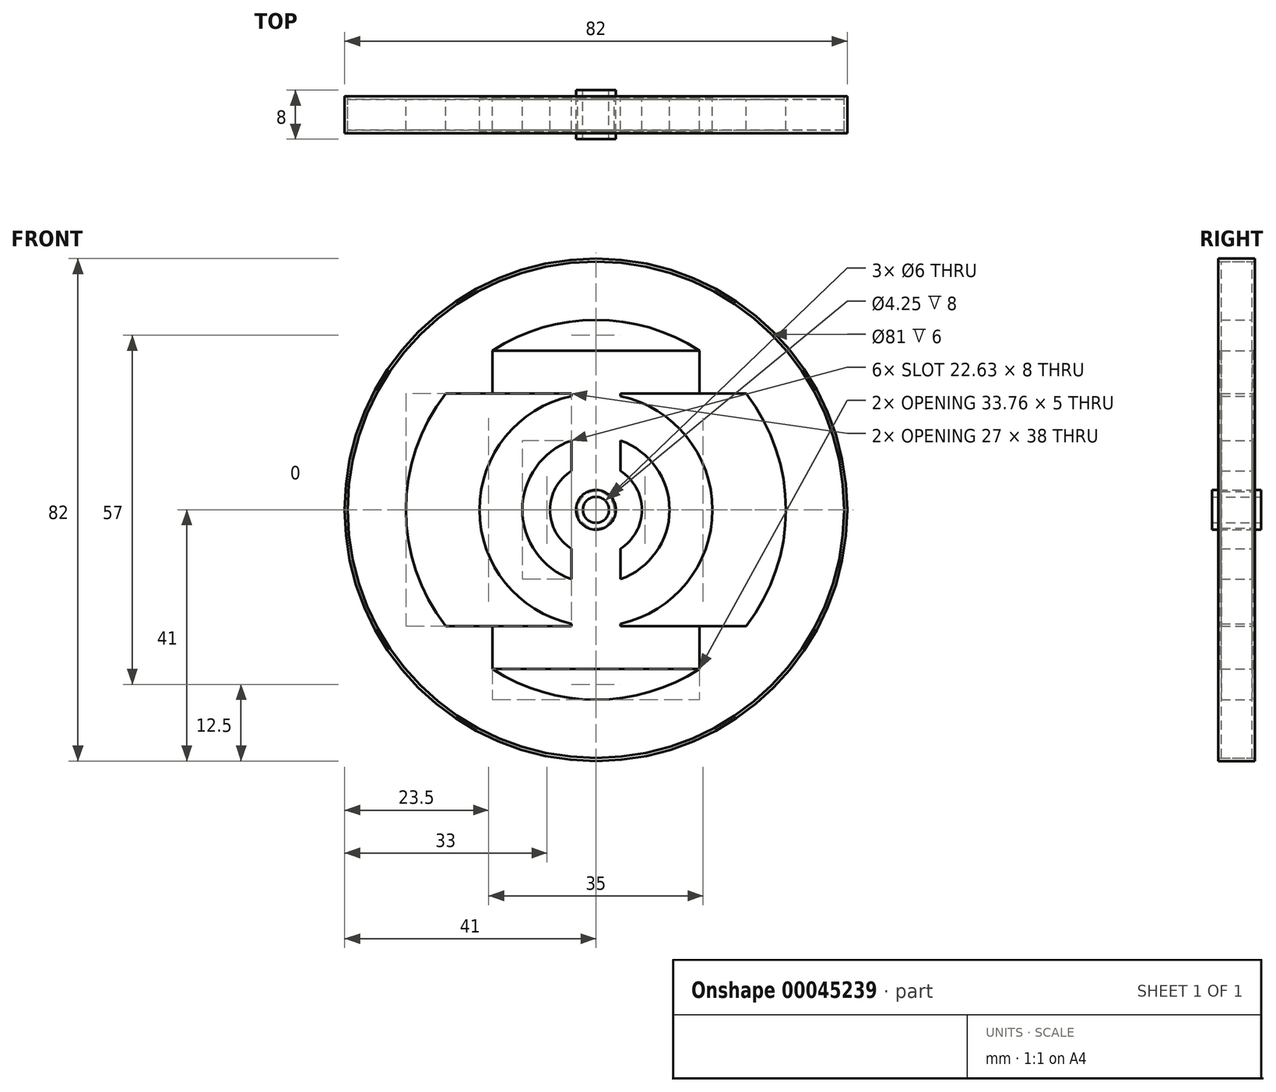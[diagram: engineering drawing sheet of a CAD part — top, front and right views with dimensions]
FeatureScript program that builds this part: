
annotation { "Feature Type Name" : "Feature", "Feature Type Description" : "" }
export const myFeature = defineFeature(function(context is Context, id is Id, definition is map)
    precondition{}
    {
        {
            var Q0;
            Q0=qCreatedBy(makeId("Front.planeOp"),FACE);
            var sketch = newSketch(context, id + "F0", { "sketchPlane" : qUnion([Q0])});
            skCircle(sketch, "E0", {"center": v(0, 0) * mm, "radius": 40.5 * mm});
            skArc(sketch, "E1", {"start": v(16.88, 26) * mm, "mid": v(0, 31) * mm, "end": v(-16.88, 26) * mm});
            skLineSegment(sketch, "E2", {"start": v(0, 40.5) * mm, "end": v(0, -40.5) * mm, "construction": true});
            skArc(sketch, "E3", {"start": v(-4, 11.31) * mm, "mid": v(-12, 0) * mm, "end": v(-4, -11.31) * mm});
            skArc(sketch, "E4", {"start": v(-4, 6.34) * mm, "mid": v(-7.5, 0) * mm, "end": v(-4, -6.34) * mm});
            skCircle(sketch, "E5", {"center": v(0, 0) * mm, "radius": 3 * mm});
            skArc(sketch, "E6", {"start": v(-4, 18.57) * mm, "mid": v(-19, 0) * mm, "end": v(-4, -18.57) * mm});
            skArc(sketch, "E7.trimOffspring", {"start": v(24.5, -19) * mm, "mid": v(31, 0) * mm, "end": v(24.5, 19) * mm});
            skArc(sketch, "E8.trimOffspring", {"start": v(4, -6.34) * mm, "mid": v(7.5, 0) * mm, "end": v(4, 6.34) * mm});
            skArc(sketch, "E9.trimOffspring", {"start": v(4, -11.31) * mm, "mid": v(12, 0) * mm, "end": v(4, 11.31) * mm});
            skLineSegment(sketch, "E10.trimOffspring", {"start": v(-4, -6.34) * mm, "end": v(-4, -11.31) * mm});
            skLineSegment(sketch, "E11.trimOffspring", {"start": v(4, -6.34) * mm, "end": v(4, -11.31) * mm});
            skLineSegment(sketch, "E12.trimOffspring", {"start": v(4, 11.31) * mm, "end": v(4, 6.34) * mm});
            skLineSegment(sketch, "E13.trimOffspring", {"start": v(-4, 11.31) * mm, "end": v(-4, 6.34) * mm});
            skLineSegment(sketch, "E14.trimOffspring", {"start": v(-4, -18.57) * mm, "end": v(-4, -19) * mm});
            skLineSegment(sketch, "E15.trimOffspring", {"start": v(4, -18.57) * mm, "end": v(4, -19) * mm});
            skLineSegment(sketch, "E16.bottom", {"start": v(-24.5, 19) * mm, "end": v(-4, 19) * mm});
            skLineSegment(sketch, "E16.top", {"start": v(-16.88, 26) * mm, "end": v(16.88, 26) * mm});
            skArc(sketch, "E17.trimOffspring", {"start": v(-24.5, 19) * mm, "mid": v(-31, 0) * mm, "end": v(-24.5, -19) * mm});
            skLineSegment(sketch, "E18.trimOffspring", {"start": v(-4, 19) * mm, "end": v(-4, 18.57) * mm});
            skLineSegment(sketch, "E19.trimOffspring", {"start": v(4, 19) * mm, "end": v(4, 18.57) * mm});
            skLineSegment(sketch, "E20.trimOffspring", {"start": v(4, 19) * mm, "end": v(24.5, 19) * mm});
            skLineSegment(sketch, "E21", {"start": v(-40.5, 0) * mm, "end": v(40.5, 0) * mm, "construction": true});
            skLineSegment(sketch, "E22.MirrorCS", {"start": v(-24.5, -19) * mm, "end": v(-4, -19) * mm});
            skLineSegment(sketch, "E23.MirrorCS", {"start": v(-16.88, -26) * mm, "end": v(16.88, -26) * mm});
            skArc(sketch, "E24.MirrorCS", {"start": v(16.88, -26) * mm, "mid": v(0, -31) * mm, "end": v(-16.88, -26) * mm});
            skLineSegment(sketch, "E25.MirrorCS", {"start": v(4, -19) * mm, "end": v(24.5, -19) * mm});
            skArc(sketch, "E26.trimOffspring", {"start": v(4, -18.57) * mm, "mid": v(19, 0) * mm, "end": v(4, 18.57) * mm});
            skPoint(sketch, "E27.trimOffspring.end.orphan", {"position": v(-16.88, -26) * mm});
            skSolve(sketch);
        }
        {
            var Q0;
            Q0=makeQuery(id+"F0.imprint","IMPRINT",FACE,{"disambiguationData":[TD([[makeQuery(id+"F0.imprint","IMPRINT",EDGE,{"derivedFrom":sQuery(id+"F0.wireOp",EDGE,"E0")}),1.0]])]});
            extrude(context, id + "F1", {"entities" : qUnion([Q0]), "endBound" : BoundingType.SYMMETRIC, "depth" : 5 * mm});
        }
        {
            var Q0;
            Q0=qCreatedBy(makeId("Front.planeOp"),FACE);
            var sketch = newSketch(context, id + "F2", { "sketchPlane" : qUnion([Q0])});
            skCircle(sketch, "E28.0", {"center": v(0, 0) * mm, "radius": 41 * mm});
            skCircle(sketch, "E29.0", {"center": v(0, 0) * mm, "radius": 40.5 * mm});
            skSolve(sketch);
        }
        {
            var Q0;
            Q0 = qSketchRegion(id + "F2", true);
            extrude(context, id + "F3", {"entities" : qUnion([Q0]), "endBound" : BoundingType.SYMMETRIC, "depth" : 6 * mm});
        }
        {
            var Q0;
            Q0=qCreatedBy(makeId("Front.planeOp"),FACE);
            var sketch = newSketch(context, id + "F4", { "sketchPlane" : qUnion([Q0])});
            skCircle(sketch, "E30", {"center": v(0, 0) * mm, "radius": 3.25 * mm});
            skCircle(sketch, "E31", {"center": v(0, 0) * mm, "radius": 2.12 * mm});
            skSolve(sketch);
        }
        {
            var Q0;
            Q0 = qSketchRegion(id + "F4", true);
            extrude(context, id + "F5", {"entities" : qUnion([Q0]), "endBound" : BoundingType.SYMMETRIC, "depth" : 8 * mm});
        }
        {
            var Q0;
            Q0=makeQuery(id+"F1.opExtrude","CAP_FACE",FACE,{"disambiguationData":[OSD([sQuery(id+"F0.wireOp",EDGE,"E0"),sQuery(id+"F0.wireOp",EDGE,"E1"),sQuery(id+"F0.wireOp",EDGE,"E3"),sQuery(id+"F0.wireOp",EDGE,"E4"),sQuery(id+"F0.wireOp",EDGE,"E5"),sQuery(id+"F0.wireOp",EDGE,"E6"),sQuery(id+"F0.wireOp",EDGE,"E7.trimOffspring"),sQuery(id+"F0.wireOp",EDGE,"E8.trimOffspring"),sQuery(id+"F0.wireOp",EDGE,"E9.trimOffspring"),sQuery(id+"F0.wireOp",EDGE,"E10.trimOffspring"),sQuery(id+"F0.wireOp",EDGE,"E11.trimOffspring"),sQuery(id+"F0.wireOp",EDGE,"E12.trimOffspring"),sQuery(id+"F0.wireOp",EDGE,"E13.trimOffspring"),sQuery(id+"F0.wireOp",EDGE,"E14.trimOffspring"),sQuery(id+"F0.wireOp",EDGE,"E15.trimOffspring"),sQuery(id+"F0.wireOp",EDGE,"E16.bottom"),sQuery(id+"F0.wireOp",EDGE,"E16.top"),sQuery(id+"F0.wireOp",EDGE,"E17.trimOffspring"),sQuery(id+"F0.wireOp",EDGE,"E18.trimOffspring"),sQuery(id+"F0.wireOp",EDGE,"E19.trimOffspring"),sQuery(id+"F0.wireOp",EDGE,"E20.trimOffspring"),sQuery(id+"F0.wireOp",EDGE,"E22.MirrorCS"),sQuery(id+"F0.wireOp",EDGE,"E23.MirrorCS"),sQuery(id+"F0.wireOp",EDGE,"E24.MirrorCS"),sQuery(id+"F0.wireOp",EDGE,"E25.MirrorCS"),sQuery(id+"F0.wireOp",EDGE,"E26.trimOffspring")])],"isStart":false});
            var sketch = newSketch(context, id + "F6", { "sketchPlane" : qUnion([Q0])});
            skLineSegment(sketch, "E32.0", {"start": v(-16.88, 26) * mm, "end": v(16.88, 26) * mm});
            skLineSegment(sketch, "E32.1", {"start": v(4, 19) * mm, "end": v(16.88, 19) * mm});
            skLineSegment(sketch, "E32.2", {"start": v(-16.88, 19) * mm, "end": v(-4, 19) * mm});
            skLineSegment(sketch, "E32.3", {"start": v(4, 19) * mm, "end": v(4, 18.57) * mm});
            skLineSegment(sketch, "E32.4", {"start": v(-4, 19) * mm, "end": v(-4, 18.57) * mm});
            skArc(sketch, "E32.5", {"start": v(-4, 18.57) * mm, "mid": v(-19, 0) * mm, "end": v(-4, -18.57) * mm});
            skArc(sketch, "E32.6", {"start": v(4, -18.57) * mm, "mid": v(19, 0) * mm, "end": v(4, 18.57) * mm});
            skArc(sketch, "E32.7", {"start": v(4, -11.31) * mm, "mid": v(12, 0) * mm, "end": v(4, 11.31) * mm});
            skLineSegment(sketch, "E32.8", {"start": v(4, 11.31) * mm, "end": v(4, 6.34) * mm});
            skLineSegment(sketch, "E32.9", {"start": v(-4, 11.31) * mm, "end": v(-4, 6.34) * mm});
            skArc(sketch, "E32.10", {"start": v(-4, 11.31) * mm, "mid": v(-12, 0) * mm, "end": v(-4, -11.31) * mm});
            skArc(sketch, "E32.11", {"start": v(-4, 6.34) * mm, "mid": v(-7.5, 0) * mm, "end": v(-4, -6.34) * mm});
            skCircle(sketch, "E32.12", {"center": v(0, 0) * mm, "radius": 3 * mm});
            skArc(sketch, "E32.13", {"start": v(4, -6.34) * mm, "mid": v(7.5, 0) * mm, "end": v(4, 6.34) * mm});
            skLineSegment(sketch, "E32.14", {"start": v(-4, -6.34) * mm, "end": v(-4, -11.31) * mm});
            skLineSegment(sketch, "E32.15", {"start": v(4, -6.34) * mm, "end": v(4, -11.31) * mm});
            skLineSegment(sketch, "E32.16", {"start": v(-16.88, -26) * mm, "end": v(16.88, -26) * mm});
            skLineSegment(sketch, "E32.17", {"start": v(-16.88, -19) * mm, "end": v(-4, -19) * mm});
            skLineSegment(sketch, "E32.18", {"start": v(-4, -18.57) * mm, "end": v(-4, -19) * mm});
            skLineSegment(sketch, "E32.19", {"start": v(4, -18.57) * mm, "end": v(4, -19) * mm});
            skLineSegment(sketch, "E32.20", {"start": v(4, -19) * mm, "end": v(16.88, -19) * mm});
            skLineSegment(sketch, "E33", {"start": v(-16.88, 26) * mm, "end": v(-16.88, 19) * mm});
            skLineSegment(sketch, "E34", {"start": v(-16.88, -26) * mm, "end": v(-16.88, -19) * mm});
            skLineSegment(sketch, "E35", {"start": v(16.88, -26) * mm, "end": v(16.88, -19) * mm});
            skLineSegment(sketch, "E36", {"start": v(16.88, 26) * mm, "end": v(16.88, 19) * mm});
            skPoint(sketch, "E37.orphan", {"position": v(-24.5, 19) * mm});
            skPoint(sketch, "E38.orphan", {"position": v(24.5, 19) * mm});
            skPoint(sketch, "E39.orphan", {"position": v(24.5, -19) * mm});
            skPoint(sketch, "E40.orphan", {"position": v(-24.5, -19) * mm});
            skSolve(sketch);
        }
        {
            var Q0;
            Q0 = qSketchRegion(id + "F6", true);
            extrude(context, id + "F7", {"entities" : qUnion([Q0]), "depth" : .25 * mm});
        }
        {
            var Q0;
            Q0=makeQuery(id+"F7.opExtrude","SWEPT_BODY",BODY,{"disambiguationData":[OSD([sQuery(id+"F6.wireOp",EDGE,"E32.0"),sQuery(id+"F6.wireOp",EDGE,"E32.1"),sQuery(id+"F6.wireOp",EDGE,"E32.2"),sQuery(id+"F6.wireOp",EDGE,"E32.3"),sQuery(id+"F6.wireOp",EDGE,"E32.4"),sQuery(id+"F6.wireOp",EDGE,"E32.5"),sQuery(id+"F6.wireOp",EDGE,"E32.6"),sQuery(id+"F6.wireOp",EDGE,"E32.7"),sQuery(id+"F6.wireOp",EDGE,"E32.8"),sQuery(id+"F6.wireOp",EDGE,"E32.9"),sQuery(id+"F6.wireOp",EDGE,"E32.10"),sQuery(id+"F6.wireOp",EDGE,"E32.11"),sQuery(id+"F6.wireOp",EDGE,"E32.12"),sQuery(id+"F6.wireOp",EDGE,"E32.13"),sQuery(id+"F6.wireOp",EDGE,"E32.14"),sQuery(id+"F6.wireOp",EDGE,"E32.15"),sQuery(id+"F6.wireOp",EDGE,"E32.16"),sQuery(id+"F6.wireOp",EDGE,"E32.17"),sQuery(id+"F6.wireOp",EDGE,"E32.18"),sQuery(id+"F6.wireOp",EDGE,"E32.19"),sQuery(id+"F6.wireOp",EDGE,"E32.20"),sQuery(id+"F6.wireOp",EDGE,"E33"),sQuery(id+"F6.wireOp",EDGE,"E34"),sQuery(id+"F6.wireOp",EDGE,"E35"),sQuery(id+"F6.wireOp",EDGE,"E36")])]});
            var Q1;
            Q1=qCreatedBy(makeId("Front.planeOp"),FACE);
            mirror(context, id + "F8", {"entities" : qUnion([Q0]), "mirrorPlane" : qUnion([Q1])});
        }
    });
